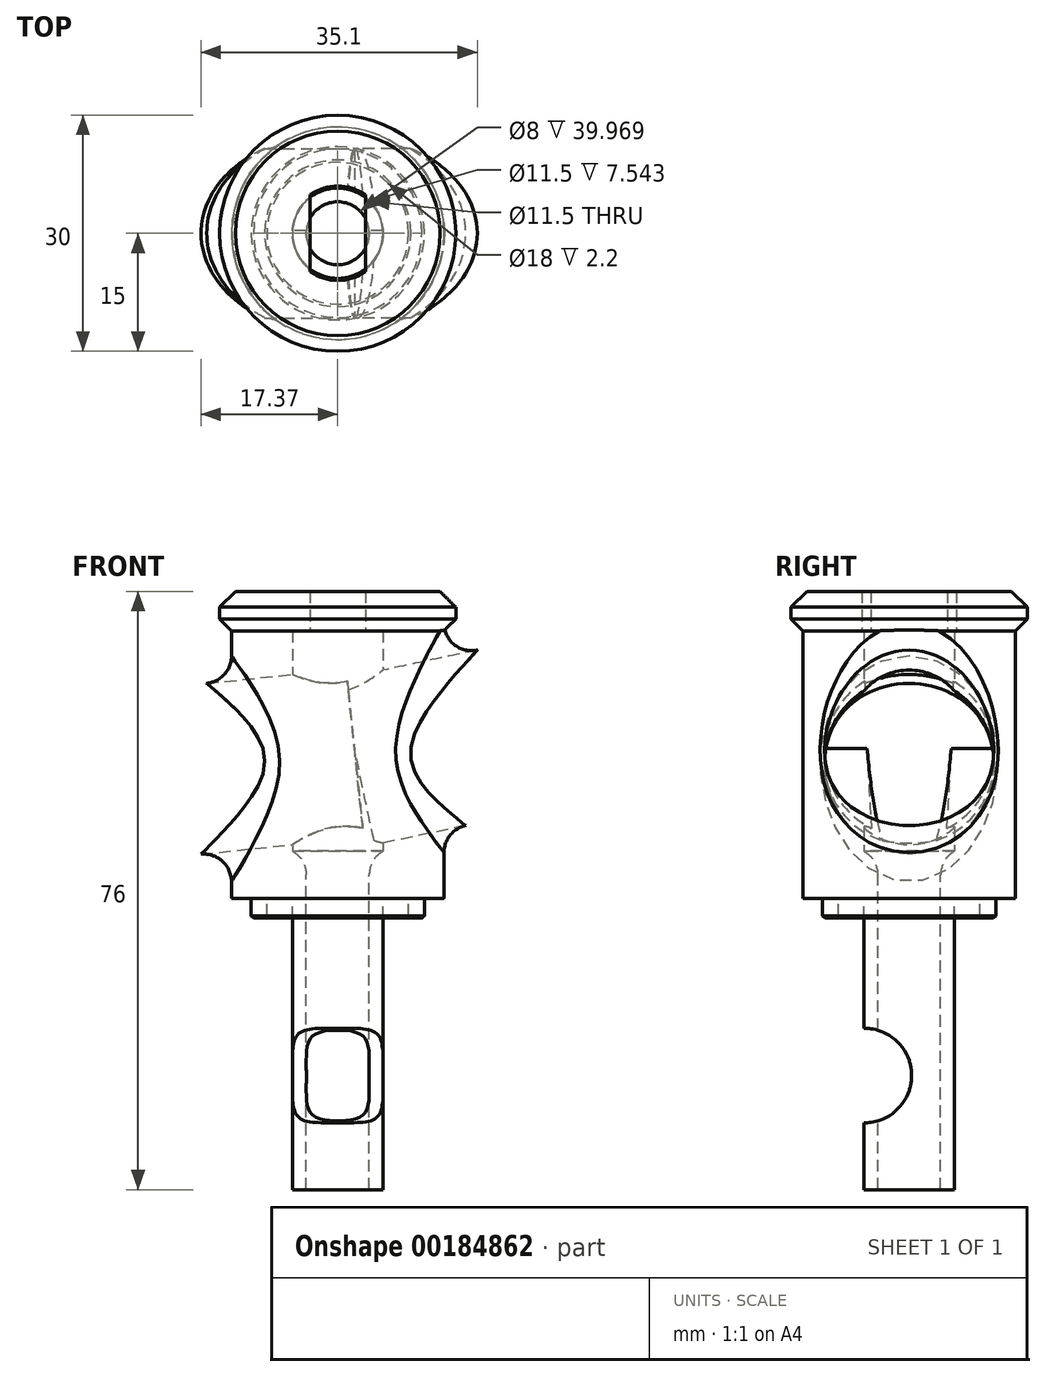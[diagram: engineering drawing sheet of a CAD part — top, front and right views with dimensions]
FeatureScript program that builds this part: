
annotation { "Feature Type Name" : "Feature", "Feature Type Description" : "" }
export const myFeature = defineFeature(function(context is Context, id is Id, definition is map)
    precondition{}
    {
        {
            var Q0;
            Q0=qCreatedBy(makeId("Top.planeOp"),FACE);
            var sketch = newSketch(context, id + "F0", { "sketchPlane" : qUnion([Q0])});
            skCircle(sketch, "E0", {"center": v(0, 0) * mm, "radius": 13.5 * mm});
            skCircle(sketch, "E1", {"center": v(0, 0) * mm, "radius": 5.75 * mm});
            skSolve(sketch);
        }
        {
            var Q0;
            Q0 = qSketchRegion(id + "F0", true);
            extrude(context, id + "F1", {"entities" : qUnion([Q0]), "depth" : 34 * mm});
        }
        {
            var Q0;
            Q0=qCreatedBy(makeId("Top.planeOp"),FACE);
            var sketch = newSketch(context, id + "F2", { "sketchPlane" : qUnion([Q0])});
            skCircle(sketch, "E2", {"center": v(0, 0) * mm, "radius": 11 * mm});
            skCircle(sketch, "E3", {"center": v(0, 0) * mm, "radius": 9 * mm});
            skSolve(sketch);
        }
        {
            var Q0;
            Q0 = qSketchRegion(id + "F2", true);
            extrude(context, id + "F3", {"entities" : qUnion([Q0]), "operationType" : NewBodyOperationType.ADD, "oppositeDirection" : true, "depth" : 2.5 * mm});
        }
        {
            var Q0;
            Q0=makeQuery(id+"F3.opExtrude","CAP_FACE",FACE,{"disambiguationData":[OSD([sQuery(id+"F2.wireOp",EDGE,"E2"),sQuery(id+"F2.wireOp",EDGE,"E3")])],"isStart":false});
            chamfer(context, id + "F4", {"entities" : qUnion([Q0]), "width" : .3 * mm, "tangentPropagation" : true});
        }
        {
            var Q0;
            Q0=qCreatedBy(makeId("Top.planeOp"),FACE);
            var sketch = newSketch(context, id + "F5", { "sketchPlane" : qUnion([Q0])});
            skCircle(sketch, "E4", {"center": v(0, 0) * mm, "radius": 15 * mm});
            skArc(sketch, "E5", {"start": v(-3.5, -4.87) * mm, "mid": v(0, -6) * mm, "end": v(3.5, -4.87) * mm});
            skLineSegment(sketch, "E6", {"start": v(6, 0) * mm, "end": v(3.5, 0) * mm});
            skLineSegment(sketch, "E7", {"start": v(-6, 0) * mm, "end": v(-3.5, 0) * mm});
            skLineSegment(sketch, "E8", {"start": v(-3.5, 4.87) * mm, "end": v(-3.5, -4.87) * mm});
            skLineSegment(sketch, "E9", {"start": v(3.5, 4.87) * mm, "end": v(3.5, -4.87) * mm});
            skArc(sketch, "E10.trimOffspring", {"start": v(3.5, 4.87) * mm, "mid": v(0, 6) * mm, "end": v(-3.5, 4.87) * mm});
            skSolve(sketch);
        }
        {
            var Q0;
            Q0 = qSketchRegion(id + "F5", true);
            extrude(context, id + "F6", {"entities" : qUnion([Q0]), "depth" : 5 * mm});
        }
        {
            var Q0;
            Q0=makeQuery(id+"F6.opExtrude","CAP_EDGE",EDGE,{"disambiguationData":[OSD([sQuery(id+"F5.wireOp",EDGE,"E4")])],"isStart":true});
            chamfer(context, id + "F7", {"entities" : qUnion([Q0]), "width" : 1.5 * mm, "tangentPropagation" : true});
        }
        {
            var Q0;
            Q0=makeQuery(id+"F6.opExtrude","CAP_EDGE",EDGE,{"disambiguationData":[OSD([sQuery(id+"F5.wireOp",EDGE,"E4")])],"isStart":false});
            chamfer(context, id + "F8", {"entities" : qUnion([Q0]), "width" : 2 * mm, "tangentPropagation" : true});
        }
        {
            var Q0;
            Q0=makeQuery(id+"F6.opExtrude","SWEPT_BODY",BODY,{"disambiguationData":[OSD([sQuery(id+"F5.wireOp",EDGE,"E4"),sQuery(id+"F5.wireOp",EDGE,"FkeDQcv7-Gxwk-BSQT-M2AH-QCBiXirRbNXo.bottom"),sQuery(id+"F5.wireOp",EDGE,"FkeDQcv7-Gxwk-BSQT-M2AH-QCBiXirRbNXo.top"),sQuery(id+"F5.wireOp",EDGE,"FkeDQcv7-Gxwk-BSQT-M2AH-QCBiXirRbNXo.left"),sQuery(id+"F5.wireOp",EDGE,"FkeDQcv7-Gxwk-BSQT-M2AH-QCBiXirRbNXo.right")])]});
            transform(context, id + "F9", {"entities" : qUnion([Q0]), "transformType" : TransformType.TRANSLATION_3D, "dx" : 0 * mm, "dy" : 0 * mm, "dz" : 34 * mm, "makeCopy" : false});
        }
        {
            var Q0;
            Q0=qCreatedBy(makeId("Right.planeOp"),FACE);
            var sketch = newSketch(context, id + "F10", { "sketchPlane" : qUnion([Q0])});
            skLineSegment(sketch, "E11", {"start": v(0, 0) * mm, "end": v(0, 18) * mm});
            skCircle(sketch, "E12", {"center": v(0, 18) * mm, "radius": 10.75 * mm});
            skSolve(sketch);
        }
        {
            var Q0;
            Q0 = qSketchRegion(id + "F10", true);
            extrude(context, id + "F11", {"entities" : qUnion([Q0]), "oppositeDirection" : true, "depth" : 25 * mm});
        }
        {
            var Q0;
            Q0=makeQuery(id+"F11.opExtrude","SWEPT_BODY",BODY,{"disambiguationData":[OSD([sQuery(id+"F10.wireOp",EDGE,"E12")])]});
            var Q1;
            Q1=makeQuery(id+"F6.opExtrude","CAP_EDGE",EDGE,{"disambiguationData":[OSD([sQuery(id+"F5.wireOp",EDGE,"E8")])],"isStart":false});
            transform(context, id + "F12", {"entities" : qUnion([Q0]), "transformType" : TransformType.ROTATION, "transformAxis" : qUnion([Q1]), "angle" : 6 * degree, "makeCopy" : false});
        }
        {
            var Q0;
            Q0=qCreatedBy(makeId("Right.planeOp"),FACE);
            var sketch = newSketch(context, id + "F13", { "sketchPlane" : qUnion([Q0])});
            skLineSegment(sketch, "E13", {"start": v(0, 0) * mm, "end": v(0, 18) * mm});
            skCircle(sketch, "E14", {"center": v(0, 18) * mm, "radius": 10.75 * mm});
            skSolve(sketch);
        }
        {
            var Q0;
            Q0 = qSketchRegion(id + "F13", true);
            extrude(context, id + "F14", {"entities" : qUnion([Q0]), "depth" : 25 * mm});
        }
        {
            var Q0;
            Q0=makeQuery(id+"F14.opExtrude","SWEPT_BODY",BODY,{"disambiguationData":[OSD([sQuery(id+"F13.wireOp",EDGE,"E14")])]});
            transform(context, id + "F15", {"entities" : qUnion([Q0]), "transformType" : TransformType.TRANSLATION_3D, "dx" : -2 * mm, "dy" : 0 * mm, "dz" : 0 * mm, "makeCopy" : false});
        }
        {
            var Q0;
            Q0=makeQuery(id+"F14.opExtrude","SWEPT_BODY",BODY,{"disambiguationData":[OSD([sQuery(id+"F13.wireOp",EDGE,"E14")])]});
            var Q1;
            Q1=makeQuery(id+"F6.opExtrude","CAP_EDGE",EDGE,{"disambiguationData":[OSD([sQuery(id+"F5.wireOp",EDGE,"E9")])],"isStart":false});
            transform(context, id + "F16", {"entities" : qUnion([Q0]), "transformType" : TransformType.ROTATION, "transformAxis" : qUnion([Q1]), "angle" : 12 * degree, "makeCopy" : false});
        }
        {
            var Q0;
            Q0=makeQuery(id+"F11.opExtrude","SWEPT_BODY",BODY,{"disambiguationData":[OSD([sQuery(id+"F10.wireOp",EDGE,"E12")])]});
            transform(context, id + "F17", {"entities" : qUnion([Q0]), "transformType" : TransformType.TRANSLATION_3D, "dx" : 0 * mm, "dy" : 0 * mm, "dz" : 0 * mm, "makeCopy" : true});
        }
        {
            var Q0;
            Q0=makeQuery(id+"F14.opExtrude","SWEPT_BODY",BODY,{"disambiguationData":[OSD([sQuery(id+"F13.wireOp",EDGE,"E14")])]});
            transform(context, id + "F18", {"entities" : qUnion([Q0]), "transformType" : TransformType.TRANSLATION_3D, "dx" : 0 * mm, "dy" : 0 * mm, "dz" : 0 * mm, "makeCopy" : true});
        }
        {
            var Q0;
            Q0=qCreatedBy(makeId("Top.planeOp"),FACE);
            var sketch = newSketch(context, id + "F19", { "sketchPlane" : qUnion([Q0])});
            skCircle(sketch, "E15", {"center": v(0, 0) * mm, "radius": 5.75 * mm});
            skCircle(sketch, "E16", {"center": v(0, 0) * mm, "radius": 4 * mm});
            skSolve(sketch);
        }
        {
            var Q0;
            Q0 = qSketchRegion(id + "F19", true);
            extrude(context, id + "F20", {"entities" : qUnion([Q0]), "operationType" : NewBodyOperationType.ADD, "oppositeDirection" : true, "depth" : 43 * mm});
        }
        {
            var Q0;
            Q0=makeQuery(id+"F20.opExtrude","SWEPT_BODY",BODY,{"disambiguationData":[OSD([sQuery(id+"F19.wireOp",EDGE,"E15"),sQuery(id+"F19.wireOp",EDGE,"E16")])]});
            transform(context, id + "F21", {"entities" : qUnion([Q0]), "transformType" : TransformType.TRANSLATION_3D, "dx" : 0 * mm, "dy" : 0 * mm, "dz" : 6 * mm, "makeCopy" : false});
        }
        {
            var Q0;
            Q0=makeQuery(id+"F1.opExtrude","SWEPT_BODY",BODY,{"disambiguationData":[OSD([sQuery(id+"F0.wireOp",EDGE,"E0"),sQuery(id+"F0.wireOp",EDGE,"E1")])]});
            var Q1;
            Q1=makeQuery(id+"F6.opExtrude","SWEPT_BODY",BODY,{"disambiguationData":[OSD([sQuery(id+"F5.wireOp",EDGE,"E4"),sQuery(id+"F5.wireOp",EDGE,"E5"),sQuery(id+"F5.wireOp",EDGE,"E8"),sQuery(id+"F5.wireOp",EDGE,"E9"),sQuery(id+"F5.wireOp",EDGE,"E10.trimOffspring")])]});
            var Q2;
            Q2=makeQuery(id+"F20.opExtrude","SWEPT_BODY",BODY,{"disambiguationData":[OSD([sQuery(id+"F19.wireOp",EDGE,"E15"),sQuery(id+"F19.wireOp",EDGE,"E16")])]});
            var Q3;
            Q3=makeQuery(id+"F11.opExtrude","SWEPT_BODY",BODY,{"disambiguationData":[OSD([sQuery(id+"F10.wireOp",EDGE,"E12")])]});
            var Q4;
            Q4=makeQuery(id+"F14.opExtrude","SWEPT_BODY",BODY,{"disambiguationData":[OSD([sQuery(id+"F13.wireOp",EDGE,"E14")])]});
            booleanBodies(context, id + "F22", {"operationType" : BooleanOperationType.UNION, "tools" : qUnion([Q0, Q1, Q2, Q3, Q4])});
        }
        {
            var Q0;
            Q0=makeQuery(id+"F22.opBoolean","INTERSECT",EDGE,{"derivedFrom":[makeQuery(id+"F1.opExtrude","SWEPT_FACE",FACE,{"disambiguationData":[OSD([sQuery(id+"F0.wireOp",EDGE,"E0")])]}),makeQuery(id+"F11.opExtrude","SWEPT_FACE",FACE,{"disambiguationData":[OSD([sQuery(id+"F10.wireOp",EDGE,"E12")])]})]});
            var Q1;
            Q1=makeQuery(id+"F22.opBoolean","INTERSECT",EDGE,{"derivedFrom":[makeQuery(id+"F1.opExtrude","SWEPT_FACE",FACE,{"disambiguationData":[OSD([sQuery(id+"F0.wireOp",EDGE,"E0")])]}),makeQuery(id+"F14.opExtrude","SWEPT_FACE",FACE,{"disambiguationData":[OSD([sQuery(id+"F13.wireOp",EDGE,"E14")])]})]});
            var Q2;
            Q2=makeQuery(id+"F20.opExtrude","CAP_EDGE",EDGE,{"disambiguationData":[OSD([sQuery(id+"F19.wireOp",EDGE,"E16")])],"isStart":true});
            fillet(context, id + "F23", {"entities" : qUnion([Q0, Q1, Q2]), "radius" : 3.5 * mm, "tangentPropagation" : true, "allowEdgeOverflow" : false});
        }
        {
            var Q0;
            Q0=qCreatedBy(makeId("Right.planeOp"),FACE);
            var sketch = newSketch(context, id + "F24", { "sketchPlane" : qUnion([Q0])});
            skLineSegment(sketch, "E17", {"start": v(-5.69, 0) * mm, "end": v(-5.69, -22.5) * mm});
            skCircle(sketch, "E18", {"center": v(-5.69, -22.5) * mm, "radius": 6 * mm});
            skSolve(sketch);
        }
        {
            var Q0;
            Q0 = qSketchRegion(id + "F24", true);
            extrude(context, id + "F25", {"entities" : qUnion([Q0]), "endBound" : BoundingType.SYMMETRIC, "depth" : 20 * mm});
        }
        {
            var Q0;
            Q0=makeQuery(id+"F25.opExtrude","SWEPT_BODY",BODY,{"disambiguationData":[OSD([sQuery(id+"F24.wireOp",EDGE,"E18")])]});
            var Q1;
            Q1=makeQuery(id+"F17.opPattern","COPY",BODY,{"derivedFrom":makeQuery(id+"F11.opExtrude","SWEPT_BODY",BODY,{"disambiguationData":[OSD([sQuery(id+"F10.wireOp",EDGE,"E12")])]}),"instanceName":"1"});
            var Q2;
            Q2=makeQuery(id+"F18.opPattern","COPY",BODY,{"derivedFrom":makeQuery(id+"F14.opExtrude","SWEPT_BODY",BODY,{"disambiguationData":[OSD([sQuery(id+"F13.wireOp",EDGE,"E14")])]}),"instanceName":"1"});
            var Q3;
            Q3=makeQuery(id+"F1.opExtrude","SWEPT_BODY",BODY,{"disambiguationData":[OSD([sQuery(id+"F0.wireOp",EDGE,"E0"),sQuery(id+"F0.wireOp",EDGE,"E1")])]});
            booleanBodies(context, id + "F26", {"operationType" : BooleanOperationType.SUBTRACTION, "tools" : qUnion([Q0, Q1, Q2]), "targets" : qUnion([Q3])});
        }
    });
